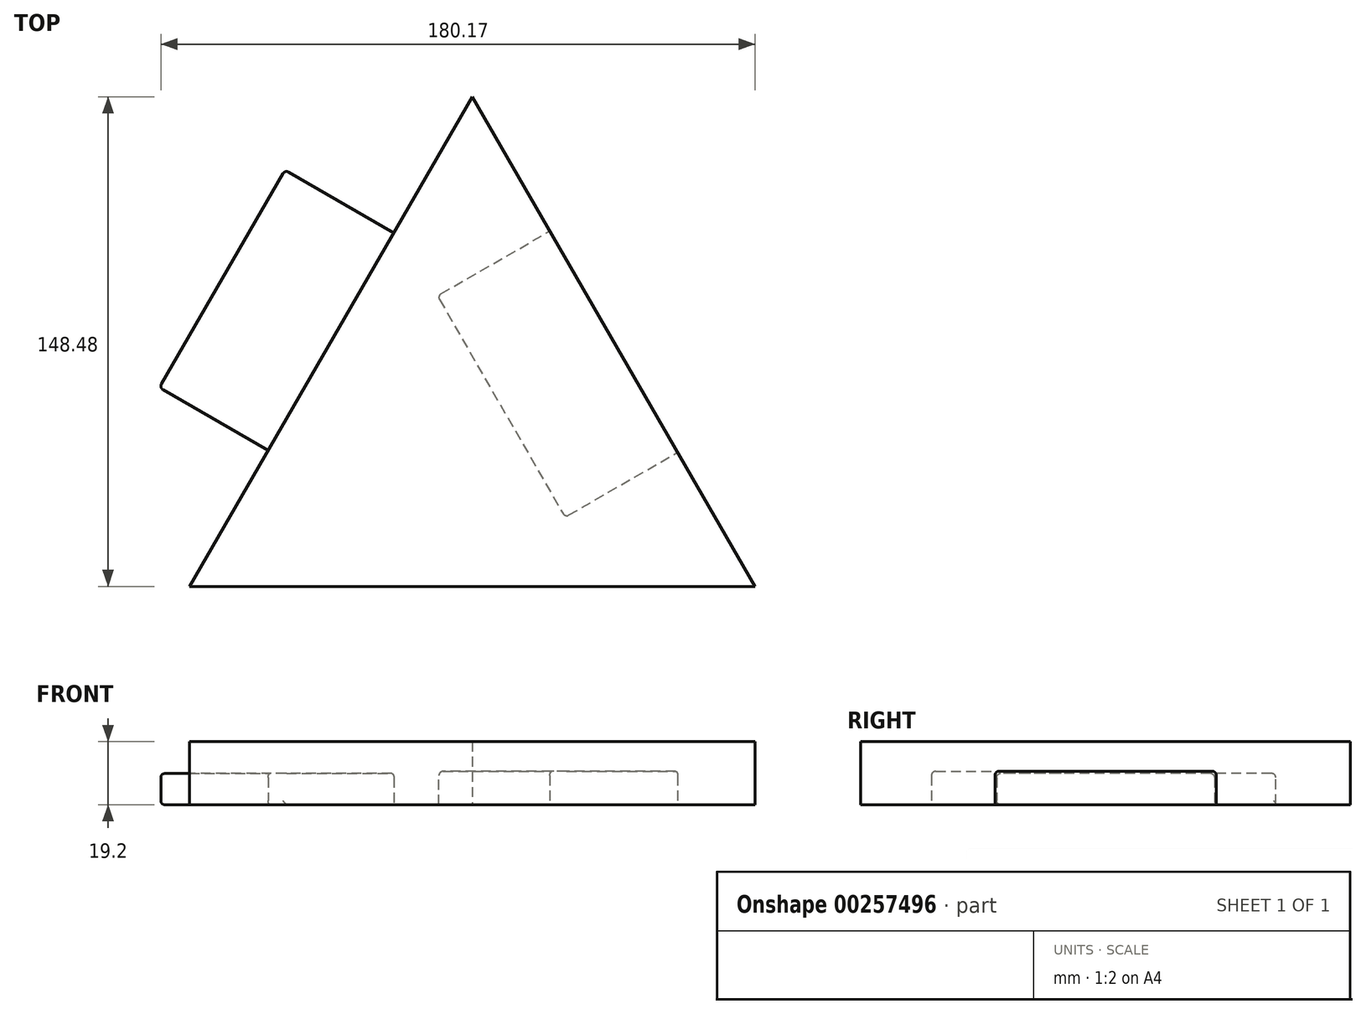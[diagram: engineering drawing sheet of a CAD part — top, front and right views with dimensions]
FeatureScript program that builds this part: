
annotation { "Feature Type Name" : "Feature", "Feature Type Description" : "" }
export const myFeature = defineFeature(function(context is Context, id is Id, definition is map)
    precondition{}
    {
        {
            var Q0;
            Q0=qCreatedBy(makeId("Top.planeOp"),FACE);
            var sketch = newSketch(context, id + "F0", { "sketchPlane" : qUnion([Q0])});
            skCircle(sketch, "E0.cCircle", {"center": v(0, 0) * mm, "radius": 49.5 * mm, "construction": true});
            skLineSegment(sketch, "E0.0", {"start": v(85.73, -49.5) * mm, "end": v(-85.73, -49.5) * mm});
            skLineSegment(sketch, "E0.1", {"start": v(-85.73, -49.5) * mm, "end": v(0, 98.99) * mm});
            skLineSegment(sketch, "E0.2", {"start": v(0, 98.99) * mm, "end": v(85.72, -49.5) * mm});
            skPoint(sketch, "E0.0.midPoint", {"position": v(0, -49.5) * mm});
            skSolve(sketch);
        }
        {
            var Q0;
            Q0=makeQuery(id+"F0.imprint","IMPRINT",FACE,{"disambiguationData":[TD([[makeQuery(id+"F0.imprint","IMPRINT",EDGE,{"derivedFrom":sQuery(id+"F0.wireOp",EDGE,"E0.0")}),-1.0]])]});
            extrude(context, id + "F1", {"entities" : qUnion([Q0]), "depth" : 19.2 * mm});
        }
        {
            var Q0;
            Q0=makeQuery(id+"F1.opExtrude","SWEPT_FACE",FACE,{"disambiguationData":[OSD([sQuery(id+"F0.wireOp",EDGE,"E0.2")])]});
            var sketch = newSketch(context, id + "F2", { "sketchPlane" : qUnion([Q0])});
            skLineSegment(sketch, "E1.bottom", {"start": v(-38.73, 10.16) * mm, "end": v(38.73, 10.16) * mm});
            skLineSegment(sketch, "E1.top", {"start": v(-38.73, 0) * mm, "end": v(38.73, 0) * mm});
            skLineSegment(sketch, "E1.left", {"start": v(-38.73, 10.16) * mm, "end": v(-38.73, 0) * mm});
            skLineSegment(sketch, "E1.right", {"start": v(38.73, 10.16) * mm, "end": v(38.73, 0) * mm});
            skSolve(sketch);
        }
        {
            var Q0;
            Q0 = qSketchRegion(id + "F2", true);
            extrude(context, id + "F3", {"entities" : qUnion([Q0]), "operationType" : NewBodyOperationType.REMOVE, "oppositeDirection" : true, "depth" : 39.37 * mm});
        }
        {
            var Q0;
            Q0=makeQuery(id+"F3.boolean.opBoolean","COPY",EDGE,{"derivedFrom":makeQuery(id+"F3.opExtrude","SWEPT_EDGE",EDGE,{"disambiguationData":[OSD([sQuery(id+"F2.wireOp",EDGE,"E1.bottom"),sQuery(id+"F2.wireOp",EDGE,"E1.left")])]})});
            var Q1;
            Q1=makeQuery(id+"F3.boolean.opBoolean","COPY",EDGE,{"derivedFrom":makeQuery(id+"F3.opExtrude","CAP_EDGE",EDGE,{"disambiguationData":[OSD([sQuery(id+"F2.wireOp",EDGE,"E1.left")])],"isStart":false})});
            var Q2;
            Q2=makeQuery(id+"F3.boolean.opBoolean","COPY",EDGE,{"derivedFrom":makeQuery(id+"F3.opExtrude","CAP_EDGE",EDGE,{"disambiguationData":[OSD([sQuery(id+"F2.wireOp",EDGE,"E1.bottom")])],"isStart":false})});
            var Q3;
            Q3=makeQuery(id+"F3.boolean.opBoolean","COPY",EDGE,{"derivedFrom":makeQuery(id+"F3.opExtrude","SWEPT_EDGE",EDGE,{"disambiguationData":[OSD([sQuery(id+"F2.wireOp",EDGE,"E1.bottom"),sQuery(id+"F2.wireOp",EDGE,"E1.right")])]})});
            var Q4;
            Q4=makeQuery(id+"F3.boolean.opBoolean","COPY",EDGE,{"derivedFrom":makeQuery(id+"F3.opExtrude","CAP_EDGE",EDGE,{"disambiguationData":[OSD([sQuery(id+"F2.wireOp",EDGE,"E1.right")])],"isStart":false})});
            var Q5;
            Q5=makeQuery(id+"F3.boolean.opBoolean","COPY",EDGE,{"derivedFrom":makeQuery(id+"F3.opExtrude","CAP_EDGE",EDGE,{"disambiguationData":[OSD([sQuery(id+"F2.wireOp",EDGE,"E1.left")])],"isStart":true})});
            fillet(context, id + "F4", {"entities" : qUnion([Q0, Q1, Q2, Q3, Q4, Q5]), "radius" : 1.27 * mm, "tangentPropagation" : true, "allowEdgeOverflow" : false});
        }
        {
            var Q0;
            Q0=makeQuery(id+"F1.opExtrude","SWEPT_FACE",FACE,{"disambiguationData":[OSD([sQuery(id+"F0.wireOp",EDGE,"E0.1")])]});
            var sketch = newSketch(context, id + "F5", { "sketchPlane" : qUnion([Q0])});
            skLineSegment(sketch, "E2.bottom", {"start": v(-38.1, 9.53) * mm, "end": v(38.1, 9.53) * mm});
            skLineSegment(sketch, "E2.top", {"start": v(-38.1, 0) * mm, "end": v(38.1, 0) * mm});
            skLineSegment(sketch, "E2.left", {"start": v(-38.1, 9.53) * mm, "end": v(-38.1, 0) * mm});
            skLineSegment(sketch, "E2.right", {"start": v(38.1, 9.53) * mm, "end": v(38.1, 0) * mm});
            skSolve(sketch);
        }
        {
            var Q0;
            Q0=makeQuery(id+"F5.imprint","IMPRINT",FACE,{"disambiguationData":[TD([[makeQuery(id+"F5.imprint","IMPRINT",EDGE,{"derivedFrom":sQuery(id+"F5.wireOp",EDGE,"E2.bottom")}),-1.0]])]});
            extrude(context, id + "F6", {"entities" : qUnion([Q0]), "operationType" : NewBodyOperationType.ADD, "depth" : 38.1 * mm});
        }
        {
            var Q0;
            Q0=makeQuery(id+"F6.opExtrude","CAP_FACE",FACE,{"disambiguationData":[OSD([sQuery(id+"F5.wireOp",EDGE,"E2.bottom"),sQuery(id+"F5.wireOp",EDGE,"E2.top"),sQuery(id+"F5.wireOp",EDGE,"E2.left"),sQuery(id+"F5.wireOp",EDGE,"E2.right")])],"isStart":false});
            var Q1;
            Q1=makeQuery(id+"F6.opExtrude","SWEPT_EDGE",EDGE,{"disambiguationData":[OSD([sQuery(id+"F5.wireOp",EDGE,"E2.bottom"),sQuery(id+"F5.wireOp",EDGE,"E2.left")])]});
            var Q2;
            Q2=makeQuery(id+"F6.opExtrude","SWEPT_EDGE",EDGE,{"disambiguationData":[OSD([sQuery(id+"F0.wireOp",EDGE,"E0.1"),sQuery(id+"F5.wireOp",EDGE,"E2.top"),sQuery(id+"F5.wireOp",EDGE,"E2.right")])]});
            var Q3;
            Q3=makeQuery(id+"F6.opExtrude","CAP_EDGE",EDGE,{"disambiguationData":[OSD([sQuery(id+"F5.wireOp",EDGE,"E2.left")])],"isStart":true});
            var Q4;
            Q4=makeQuery(id+"F6.opExtrude","CAP_EDGE",EDGE,{"disambiguationData":[OSD([sQuery(id+"F5.wireOp",EDGE,"E2.right")])],"isStart":true});
            var Q5;
            Q5=makeQuery(id+"F6.opExtrude","SWEPT_EDGE",EDGE,{"disambiguationData":[OSD([sQuery(id+"F5.wireOp",EDGE,"E2.bottom"),sQuery(id+"F5.wireOp",EDGE,"E2.right")])]});
            fillet(context, id + "F7", {"entities" : qUnion([Q0, Q1, Q2, Q3, Q4, Q5]), "radius" : 1.27 * mm, "tangentPropagation" : true, "allowEdgeOverflow" : false});
        }
    });
